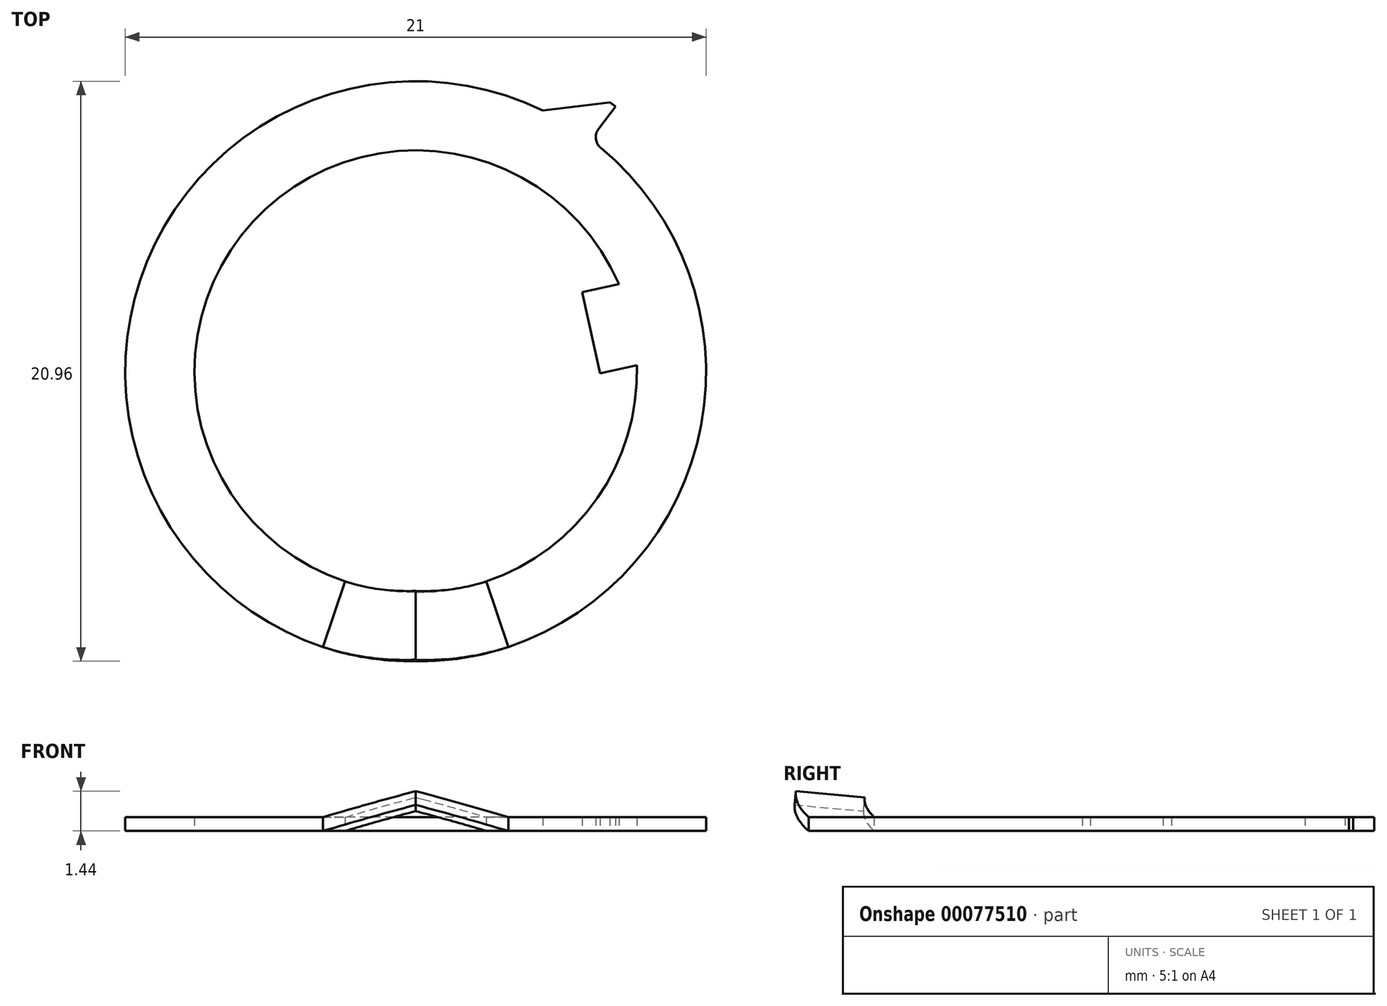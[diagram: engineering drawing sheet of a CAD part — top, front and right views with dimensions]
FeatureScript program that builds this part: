
annotation { "Feature Type Name" : "Feature", "Feature Type Description" : "" }
export const myFeature = defineFeature(function(context is Context, id is Id, definition is map)
    precondition{}
    {
        {
            var Q0;
            Q0=qCreatedBy(makeId("Top.planeOp"),FACE);
            var sketch = newSketch(context, id + "F0", { "sketchPlane" : qUnion([Q0])});
            skArc(sketch, "E0", {"start": v(4.6, 9.44) * mm, "mid": v(-9.71, 3.98) * mm, "end": v(-3.35, -9.95) * mm});
            skArc(sketch, "E1", {"start": v(7.35, 3.17) * mm, "mid": v(-5.88, 5.42) * mm, "end": v(-2.55, -7.58) * mm});
            skLineSegment(sketch, "E2", {"start": v(0, 0) * mm, "end": v(6.35, 1.4) * mm, "construction": true});
            skLineSegment(sketch, "E3", {"start": v(6.67, -0.06) * mm, "end": v(6.02, 2.87) * mm});
            skLineSegment(sketch, "E4", {"start": v(6.67, -0.06) * mm, "end": v(8, 0.24) * mm});
            skLineSegment(sketch, "E5", {"start": v(6.02, 2.87) * mm, "end": v(7.35, 3.17) * mm});
            skLineSegment(sketch, "E6", {"start": v(6.61, 8.78) * mm, "end": v(7.22, 9.58) * mm});
            skArc(sketch, "E7", {"start": v(7.22, 9.58) * mm, "mid": v(7.12, 9.66) * mm, "end": v(7.02, 9.73) * mm});
            skLineSegment(sketch, "E8", {"start": v(7.02, 9.73) * mm, "end": v(4.6, 9.44) * mm});
            skLineSegment(sketch, "E9", {"start": v(4.6, 9.44) * mm, "end": v(0, 0) * mm, "construction": true});
            skLineSegment(sketch, "E10", {"start": v(6.32, 8.39) * mm, "end": v(0, 0) * mm, "construction": true});
            skArc(sketch, "E11", {"start": v(6.61, 8.78) * mm, "mid": v(6.52, 8.42) * mm, "end": v(6.7, 8.09) * mm});
            skLineSegment(sketch, "E12", {"start": v(3.35, -9.95) * mm, "end": v(2.55, -7.58) * mm});
            skLineSegment(sketch, "E13", {"start": v(-3.35, -9.95) * mm, "end": v(-2.55, -7.58) * mm});
            skArc(sketch, "E14.trimOffspring", {"start": v(2.55, -7.58) * mm, "mid": v(6.57, -4.57) * mm, "end": v(8, 0.24) * mm});
            skArc(sketch, "E15.trimOffspring", {"start": v(3.35, -9.95) * mm, "mid": v(10.32, -1.91) * mm, "end": v(6.7, 8.09) * mm});
            skSolve(sketch);
        }
        {
            var Q0;
            Q0=makeQuery(id+"F0.imprint","IMPRINT",FACE,{"disambiguationData":[TD([[makeQuery(id+"F0.imprint","IMPRINT",EDGE,{"derivedFrom":sQuery(id+"F0.wireOp",EDGE,"E0")}),1.0]])]});
            extrude(context, id + "F1", {"entities" : qUnion([Q0]), "depth" : 0.5 * mm});
        }
        {
            var Q0;
            Q0=makeQuery(id+"F1.opExtrude","CAP_EDGE",EDGE,{"disambiguationData":[OSD([sQuery(id+"F0.wireOp",EDGE,"E12")])],"isStart":true});
            cPlane(context, id + "F2", {"entities" : qUnion([Q0]), "cplaneType" : CPlaneType.LINE_ANGLE, "offset" : 150 * mm, "angle" : 15.77 * degree, "width" : 150 * mm, "height" : 150 * mm});
        }
        {
            var Q0;
            Q0=qCreatedBy(id+"F2.planeOp",FACE);
            var sketch = newSketch(context, id + "F3", { "sketchPlane" : qUnion([Q0])});
            skArc(sketch, "E16", {"start": v(0, -8) * mm, "mid": v(1.34, -7.89) * mm, "end": v(2.64, -7.55) * mm});
            skArc(sketch, "E17", {"start": v(0, -10.5) * mm, "mid": v(1.76, -10.35) * mm, "end": v(3.47, -9.91) * mm});
            skLineSegment(sketch, "E18", {"start": v(2.64, -7.55) * mm, "end": v(3.47, -9.91) * mm});
            skLineSegment(sketch, "E19", {"start": v(0, -8) * mm, "end": v(0, -10.5) * mm});
            skSolve(sketch);
        }
        {
            var Q0;
            Q0=makeQuery(id+"F1.opExtrude","CAP_EDGE",EDGE,{"disambiguationData":[OSD([sQuery(id+"F0.wireOp",EDGE,"E13")])],"isStart":true});
            cPlane(context, id + "F4", {"entities" : qUnion([Q0]), "cplaneType" : CPlaneType.LINE_ANGLE, "offset" : 150 * mm, "angle" : 164.23 * degree, "width" : 150 * mm, "height" : 150 * mm});
        }
        {
            var Q0;
            Q0=qCreatedBy(id+"F4.planeOp",FACE);
            var sketch = newSketch(context, id + "F5", { "sketchPlane" : qUnion([Q0])});
            skArc(sketch, "E20", {"start": v(0, 8) * mm, "mid": v(-1.34, 7.89) * mm, "end": v(-2.64, 7.55) * mm});
            skArc(sketch, "E21", {"start": v(0, 10.5) * mm, "mid": v(-1.76, 10.35) * mm, "end": v(-3.47, 9.91) * mm});
            skLineSegment(sketch, "E22", {"start": v(-2.64, 7.55) * mm, "end": v(-3.47, 9.91) * mm});
            skLineSegment(sketch, "E23", {"start": v(0, 8) * mm, "end": v(0, 10.5) * mm});
            skSolve(sketch);
        }
        {
            var Q0;
            Q0=makeQuery(id+"F1.opExtrude","SWEPT_FACE",FACE,{"disambiguationData":[OSD([sQuery(id+"F0.wireOp",EDGE,"E13")])]});
            var Q1;
            Q1=sQuery(id+"F5.wireOp",EDGE,"E21");
            var Q2;
            Q2=sQuery(id+"F3.wireOp",EDGE,"E17");
            sweep(context, id + "F6", {"operationType" : NewBodyOperationType.ADD, "profiles" : qUnion([Q0]), "path" : qUnion([Q1, Q2])});
        }
    });
